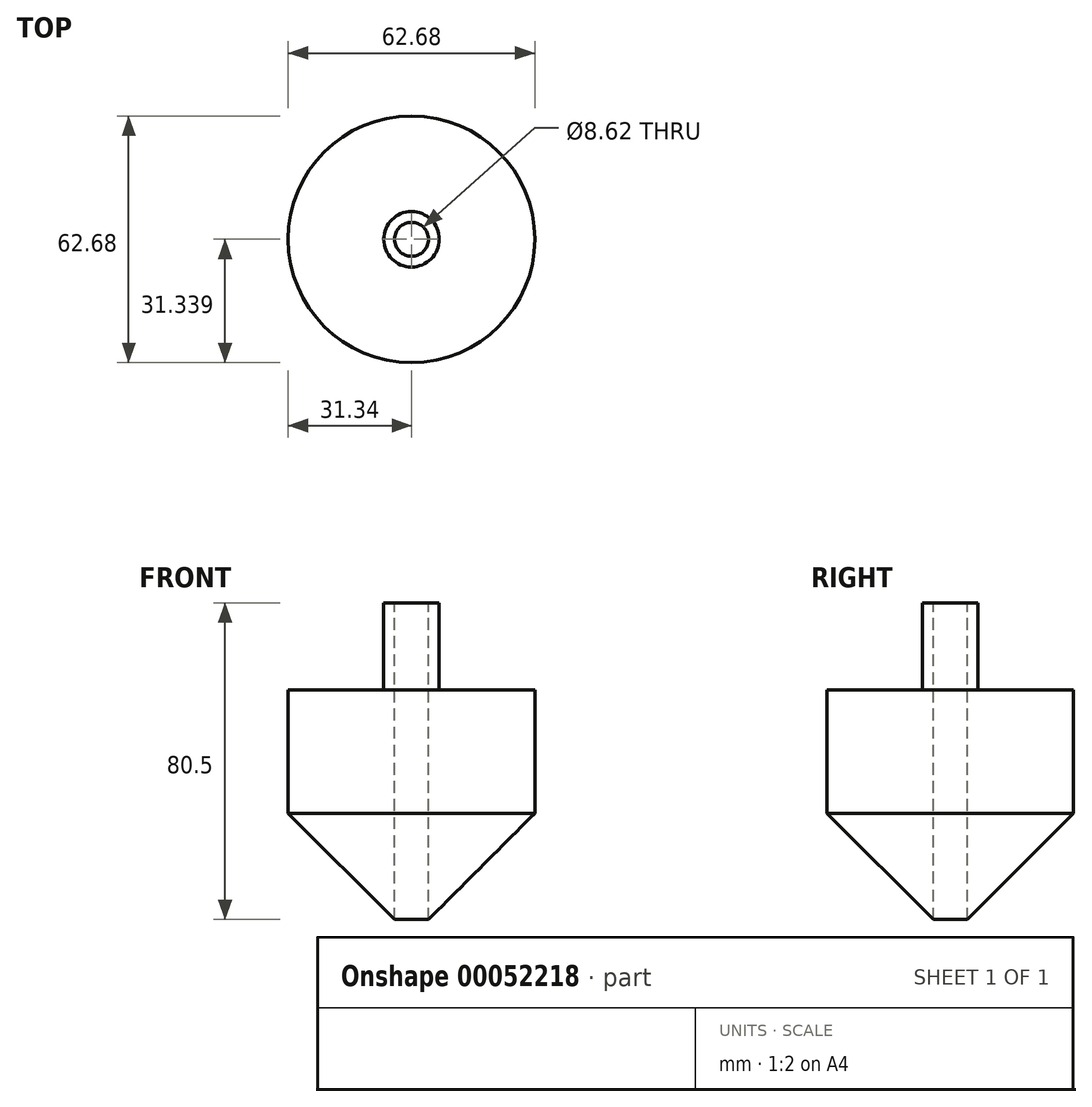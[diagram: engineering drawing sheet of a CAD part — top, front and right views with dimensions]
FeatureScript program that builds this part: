
annotation { "Feature Type Name" : "Feature", "Feature Type Description" : "" }
export const myFeature = defineFeature(function(context is Context, id is Id, definition is map)
    precondition{}
    {
        {
            var Q0;
            Q0=qCreatedBy(makeId("Right.planeOp"),FACE);
            var sketch = newSketch(context, id + "F0", { "sketchPlane" : qUnion([Q0])});
            skLineSegment(sketch, "E0", {"start": v(0, 37.12) * mm, "end": v(-2.74, 37.12) * mm});
            skLineSegment(sketch, "E1", {"start": v(-2.74, 37.12) * mm, "end": v(-2.74, 14.98) * mm});
            skLineSegment(sketch, "E2", {"start": v(-2.74, 14.98) * mm, "end": v(-27.03, 14.98) * mm});
            skLineSegment(sketch, "E3", {"start": v(-27.03, 14.98) * mm, "end": v(-27.03, -16.35) * mm});
            skLineSegment(sketch, "E4", {"start": v(-27.03, -16.35) * mm, "end": v(0, -43.38) * mm});
            skLineSegment(sketch, "E5", {"start": v(0, 37.12) * mm, "end": v(0, -43.38) * mm});
            skLineSegment(sketch, "E6", {"start": v(-3.33, 13.02) * mm, "end": v(-24.87, 13.02) * mm});
            skLineSegment(sketch, "E7", {"start": v(-24.87, 13.02) * mm, "end": v(-24.87, -14.4) * mm});
            skLineSegment(sketch, "E8", {"start": v(-24.87, -14.4) * mm, "end": v(-2.25, -37.02) * mm});
            skLineSegment(sketch, "E9", {"start": v(4.3, 37.12) * mm, "end": v(4.3, -43.38) * mm});
            skSolve(sketch);
        }
        {
            var Q0;
            Q0 = qSketchRegion(id + "F0", true);
            var Q1;
            Q1=sQuery(id+"F0.wireOp",EDGE,"E9");
            revolve(context, id + "F1", {"entities" : qUnion([Q0]), "axis" : qUnion([Q1]), "revolveType" : RevolveType.FULL});
        }
    });
